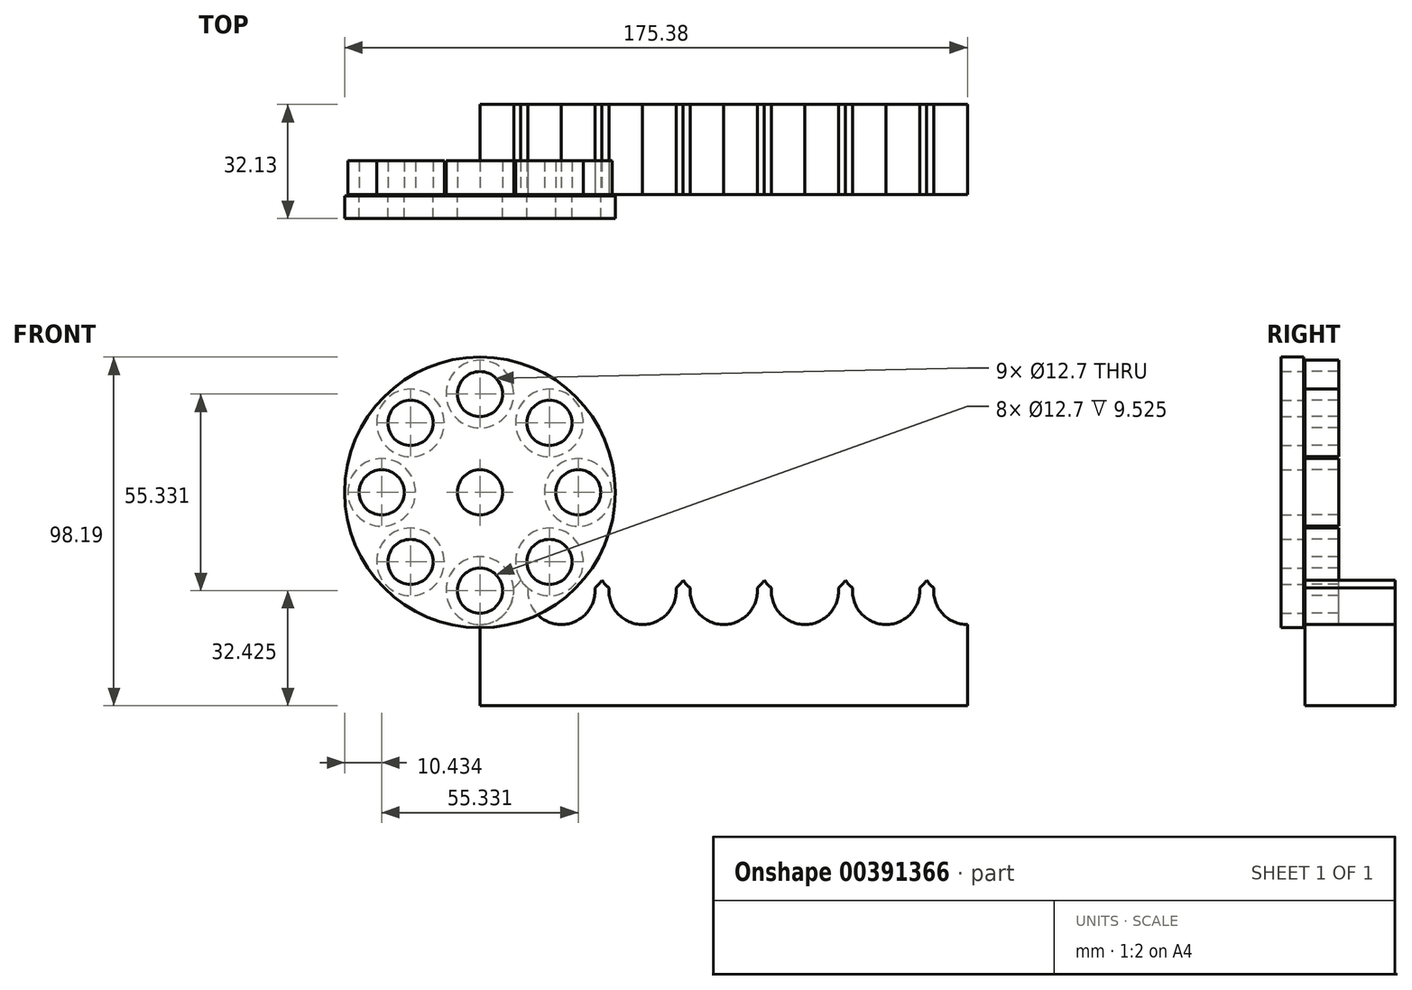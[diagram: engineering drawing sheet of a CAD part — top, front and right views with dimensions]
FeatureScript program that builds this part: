
annotation { "Feature Type Name" : "Feature", "Feature Type Description" : "" }
export const myFeature = defineFeature(function(context is Context, id is Id, definition is map)
    precondition{}
    {
        {
            var Q0;
            Q0=qCreatedBy(makeId("Front.planeOp"),FACE);
            var sketch = newSketch(context, id + "F0", { "sketchPlane" : qUnion([Q0])});
            skCircle(sketch, "E0", {"center": v(0, 0) * mm, "radius": 38.1 * mm});
            skCircle(sketch, "E1", {"center": v(27.67, 0) * mm, "radius": 6.35 * mm});
            skCircle(sketch, "E2", {"center": v(0, 0) * mm, "radius": 6.35 * mm});
            skCircle(sketch, "E3.1.0", {"center": v(19.56, 19.56) * mm, "radius": 6.35 * mm});
            skCircle(sketch, "E3.2.0", {"center": v(0, 27.67) * mm, "radius": 6.35 * mm});
            skCircle(sketch, "E3.3.0", {"center": v(-19.56, 19.56) * mm, "radius": 6.35 * mm});
            skCircle(sketch, "E3.4.0", {"center": v(-27.67, 0) * mm, "radius": 6.35 * mm});
            skCircle(sketch, "E3.5.0", {"center": v(-19.56, -19.56) * mm, "radius": 6.35 * mm});
            skCircle(sketch, "E3.6.0", {"center": v(0, -27.67) * mm, "radius": 6.35 * mm});
            skCircle(sketch, "E3.7.0", {"center": v(19.56, -19.56) * mm, "radius": 6.35 * mm});
            skCircle(sketch, "E4", {"center": v(27.67, 0) * mm, "radius": 9.53 * mm, "construction": true});
            skCircle(sketch, "E5.1.0", {"center": v(19.56, 19.56) * mm, "radius": 9.52 * mm, "construction": true});
            skCircle(sketch, "E5.2.0", {"center": v(0, 27.67) * mm, "radius": 9.53 * mm, "construction": true});
            skCircle(sketch, "E6.1.3.0", {"center": v(-19.56, 19.56) * mm, "radius": 9.53 * mm, "construction": true});
            skCircle(sketch, "E7.1.4.0", {"center": v(-27.67, 0) * mm, "radius": 9.53 * mm, "construction": true});
            skCircle(sketch, "E8.1.5.0", {"center": v(-19.56, -19.56) * mm, "radius": 9.53 * mm, "construction": true});
            skCircle(sketch, "E9.1.6.0", {"center": v(0, -27.67) * mm, "radius": 9.53 * mm, "construction": true});
            skCircle(sketch, "E10.1.7.0", {"center": v(19.56, -19.56) * mm, "radius": 9.53 * mm, "construction": true});
            skLineSegment(sketch, "E11", {"start": v(35.2, -14.58) * mm, "end": v(-35.2, 14.58) * mm, "construction": true});
            skLineSegment(sketch, "E12", {"start": v(19.56, -19.56) * mm, "end": v(27.67, 0) * mm, "construction": true});
            skPoint(sketch, "E13", {"position": v(23.61, -9.78) * mm});
            skSolve(sketch);
        }
        {
            var Q0;
            Q0 = qSketchRegion(id + "F0", true);
            extrude(context, id + "F1", {"entities" : qUnion([Q0]), "depth" : 6.35 * mm, "offsetDistance" : 25.4 * mm});
        }
        {
            var Q0;
            Q0=makeQuery(id+"F0.imprint","IMPRINT",FACE,{"disambiguationData":[TD([[makeQuery(id+"F0.imprint","IMPRINT",EDGE,{"derivedFrom":sQuery(id+"F0.wireOp",EDGE,"E0")}),1.0]])]});
            cPlane(context, id + "F2", {"entities" : qUnion([Q0]), "cplaneType" : CPlaneType.OFFSET, "offset" : 0.38 * mm, "oppositeDirection" : true, "width" : 152.4 * mm, "height" : 152.4 * mm});
        }
        {
            var Q0;
            Q0=qCreatedBy(id+"F2.planeOp",FACE);
            var sketch = newSketch(context, id + "F3", { "sketchPlane" : qUnion([Q0])});
            skCircle(sketch, "E14.0", {"center": v(0, -27.67) * mm, "radius": 9.53 * mm});
            skCircle(sketch, "E14.1", {"center": v(19.56, -19.56) * mm, "radius": 9.53 * mm});
            skCircle(sketch, "E14.2", {"center": v(27.67, 0) * mm, "radius": 9.53 * mm});
            skCircle(sketch, "E14.3", {"center": v(19.56, 19.56) * mm, "radius": 9.52 * mm});
            skCircle(sketch, "E14.4", {"center": v(0, 27.67) * mm, "radius": 9.53 * mm});
            skCircle(sketch, "E14.5", {"center": v(-19.56, 19.56) * mm, "radius": 9.53 * mm});
            skCircle(sketch, "E14.6", {"center": v(-27.67, 0) * mm, "radius": 9.53 * mm});
            skCircle(sketch, "E14.7", {"center": v(-19.56, -19.56) * mm, "radius": 9.53 * mm});
            skCircle(sketch, "E15.0", {"center": v(19.56, -19.56) * mm, "radius": 6.35 * mm});
            skCircle(sketch, "E15.1", {"center": v(0, -27.67) * mm, "radius": 6.35 * mm});
            skCircle(sketch, "E15.2", {"center": v(27.67, 0) * mm, "radius": 6.35 * mm});
            skCircle(sketch, "E15.3", {"center": v(19.56, 19.56) * mm, "radius": 6.35 * mm});
            skCircle(sketch, "E15.4", {"center": v(0, 27.67) * mm, "radius": 6.35 * mm});
            skCircle(sketch, "E15.5", {"center": v(-19.56, 19.56) * mm, "radius": 6.35 * mm});
            skCircle(sketch, "E15.6", {"center": v(-27.67, 0) * mm, "radius": 6.35 * mm});
            skCircle(sketch, "E15.7", {"center": v(-19.56, -19.56) * mm, "radius": 6.35 * mm});
            skSolve(sketch);
        }
        {
            var Q0;
            Q0 = qSketchRegion(id + "F3", true);
            extrude(context, id + "F4", {"entities" : qUnion([Q0]), "oppositeDirection" : true, "depth" : 9.52 * mm, "offsetDistance" : 25.4 * mm});
        }
        {
            var Q0;
            Q0=qCreatedBy(id+"F2.planeOp",FACE);
            var sketch = newSketch(context, id + "F5", { "sketchPlane" : qUnion([Q0])});
            skCircle(sketch, "E16", {"center": v(0, 0) * mm, "radius": 29.52 * mm, "construction": true});
            skArc(sketch, "E17.1.0.0", {"start": v(13.46, -26.91) * mm, "mid": v(15.97, -34.15) * mm, "end": v(22.98, -37.22) * mm});
            skLineSegment(sketch, "E17.direction1", {"start": v(0, -26.91) * mm, "end": v(13.46, -26.91) * mm, "construction": true});
            skArc(sketch, "E18", {"start": v(11.5, -24.67) * mm, "mid": v(12.37, -25.88) * mm, "end": v(13.46, -26.91) * mm});
            skArc(sketch, "E19", {"start": v(9.52, -26.91) * mm, "mid": v(10.6, -25.88) * mm, "end": v(11.5, -24.67) * mm});
            skLineSegment(sketch, "E20", {"start": v(13.46, -26.91) * mm, "end": v(9.52, -26.91) * mm, "construction": true});
            skLineSegment(sketch, "E21", {"start": v(11.5, -24.67) * mm, "end": v(11.5, -26.91) * mm, "construction": true});
            skLineSegment(sketch, "E22", {"start": v(11.5, -26.91) * mm, "end": v(11.5, -25.79) * mm});
            skLineSegment(sketch, "E23", {"start": v(0, 0) * mm, "end": v(0, -44.63) * mm, "construction": true});
            skArc(sketch, "E24.trimOffspring", {"start": v(0, -37.22) * mm, "mid": v(7.01, -34.15) * mm, "end": v(9.52, -26.91) * mm});
            skPoint(sketch, "E25.orphan", {"position": v(32.5, -26.91) * mm});
            skArc(sketch, "E26.1.0.0", {"start": v(36.32, -26.91) * mm, "mid": v(38.83, -34.15) * mm, "end": v(45.84, -37.22) * mm});
            skArc(sketch, "E26.1.0.1", {"start": v(22.86, -37.22) * mm, "mid": v(29.87, -34.15) * mm, "end": v(32.38, -26.91) * mm});
            skArc(sketch, "E26.1.0.2", {"start": v(34.35, -24.67) * mm, "mid": v(35.23, -25.88) * mm, "end": v(36.32, -26.91) * mm});
            skArc(sketch, "E26.1.0.3", {"start": v(32.38, -26.91) * mm, "mid": v(33.47, -25.88) * mm, "end": v(34.35, -24.67) * mm});
            skArc(sketch, "E26.2.0.0", {"start": v(59.18, -26.91) * mm, "mid": v(61.69, -34.15) * mm, "end": v(68.7, -37.22) * mm});
            skArc(sketch, "E26.2.0.1", {"start": v(45.72, -37.22) * mm, "mid": v(52.73, -34.15) * mm, "end": v(55.24, -26.91) * mm});
            skArc(sketch, "E26.2.0.2", {"start": v(57.21, -24.67) * mm, "mid": v(58.1, -25.88) * mm, "end": v(59.18, -26.91) * mm});
            skArc(sketch, "E26.2.0.3", {"start": v(55.24, -26.91) * mm, "mid": v(56.33, -25.88) * mm, "end": v(57.21, -24.67) * mm});
            skArc(sketch, "E26.3.0.0", {"start": v(82.04, -26.91) * mm, "mid": v(84.55, -34.15) * mm, "end": v(91.56, -37.22) * mm});
            skArc(sketch, "E26.3.0.1", {"start": v(68.58, -37.22) * mm, "mid": v(75.6, -34.15) * mm, "end": v(78.1, -26.91) * mm});
            skArc(sketch, "E26.3.0.2", {"start": v(80.07, -24.67) * mm, "mid": v(80.95, -25.88) * mm, "end": v(82.04, -26.91) * mm});
            skArc(sketch, "E26.3.0.3", {"start": v(78.1, -26.91) * mm, "mid": v(79.19, -25.88) * mm, "end": v(80.07, -24.67) * mm});
            skArc(sketch, "E26.4.0.0", {"start": v(104.9, -26.91) * mm, "mid": v(107.4, -34.15) * mm, "end": v(114.42, -37.22) * mm});
            skArc(sketch, "E26.4.0.1", {"start": v(91.44, -37.22) * mm, "mid": v(98.45, -34.15) * mm, "end": v(100.96, -26.91) * mm});
            skArc(sketch, "E26.4.0.2", {"start": v(102.93, -24.67) * mm, "mid": v(103.81, -25.88) * mm, "end": v(104.9, -26.91) * mm});
            skArc(sketch, "E26.4.0.3", {"start": v(100.96, -26.91) * mm, "mid": v(102.05, -25.88) * mm, "end": v(102.93, -24.67) * mm});
            skArc(sketch, "E26.5.0.0", {"start": v(127.76, -26.91) * mm, "mid": v(130.27, -34.15) * mm, "end": v(137.28, -37.22) * mm});
            skArc(sketch, "E26.5.0.1", {"start": v(114.3, -37.22) * mm, "mid": v(121.31, -34.15) * mm, "end": v(123.82, -26.91) * mm});
            skArc(sketch, "E26.5.0.2", {"start": v(125.8, -24.67) * mm, "mid": v(126.67, -25.88) * mm, "end": v(127.76, -26.91) * mm});
            skArc(sketch, "E26.5.0.3", {"start": v(123.82, -26.91) * mm, "mid": v(124.9, -25.88) * mm, "end": v(125.8, -24.67) * mm});
            skLineSegment(sketch, "E26.direction1", {"start": v(22.98, -37.22) * mm, "end": v(45.84, -37.22) * mm, "construction": true});
            skLineSegment(sketch, "E27", {"start": v(137.28, -37.22) * mm, "end": v(137.28, -60.09) * mm});
            skLineSegment(sketch, "E28", {"start": v(137.28, -60.09) * mm, "end": v(0, -60.09) * mm});
            skLineSegment(sketch, "E29", {"start": v(0, -60.09) * mm, "end": v(0, -37.22) * mm});
            skSolve(sketch);
        }
        {
            var Q0;
            Q0 = qSketchRegion(id + "F5", true);
            extrude(context, id + "F6", {"entities" : qUnion([Q0]), "oppositeDirection" : true, "depth" : 25.4 * mm, "offsetDistance" : 25.4 * mm});
        }
    });
